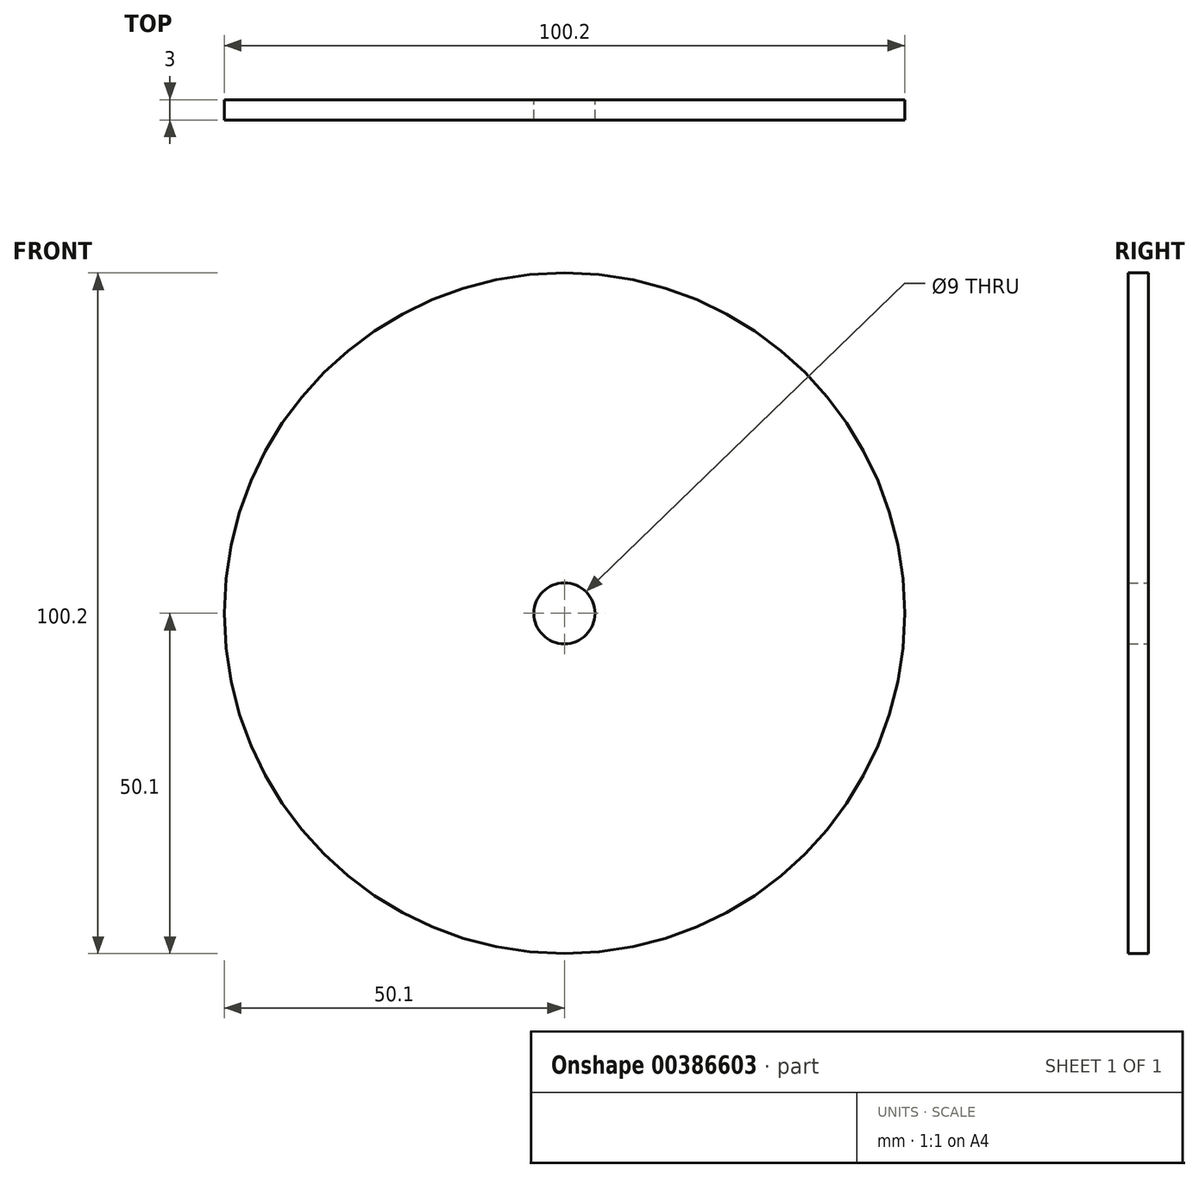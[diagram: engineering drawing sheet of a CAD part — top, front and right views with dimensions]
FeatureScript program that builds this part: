
annotation { "Feature Type Name" : "Feature", "Feature Type Description" : "" }
export const myFeature = defineFeature(function(context is Context, id is Id, definition is map)
    precondition{}
    {
        {
            var Q0;
            Q0=qCreatedBy(makeId("Front.planeOp"),FACE);
            var sketch = newSketch(context, id + "F0", { "sketchPlane" : qUnion([Q0])});
            skCircle(sketch, "E0", {"center": v(0, 0) * mm, "radius": 50.1 * mm});
            skCircle(sketch, "E1", {"center": v(0, 0) * mm, "radius": 4.5 * mm});
            skSolve(sketch);
        }
        {
            var Q0;
            Q0=sQuery(id+"F0.wireOp",EDGE,"E0");
            extrude(context, id + "F1", {"bodyType" : ToolBodyType.SURFACE, "surfaceEntities" : qUnion([Q0]), "depth" : 2 * mm});
        }
        {
            var Q0;
            Q0 = qSketchRegion(id + "F0", true);
            extrude(context, id + "F2", {"entities" : qUnion([Q0]), "depth" : 3 * mm});
        }
    });
